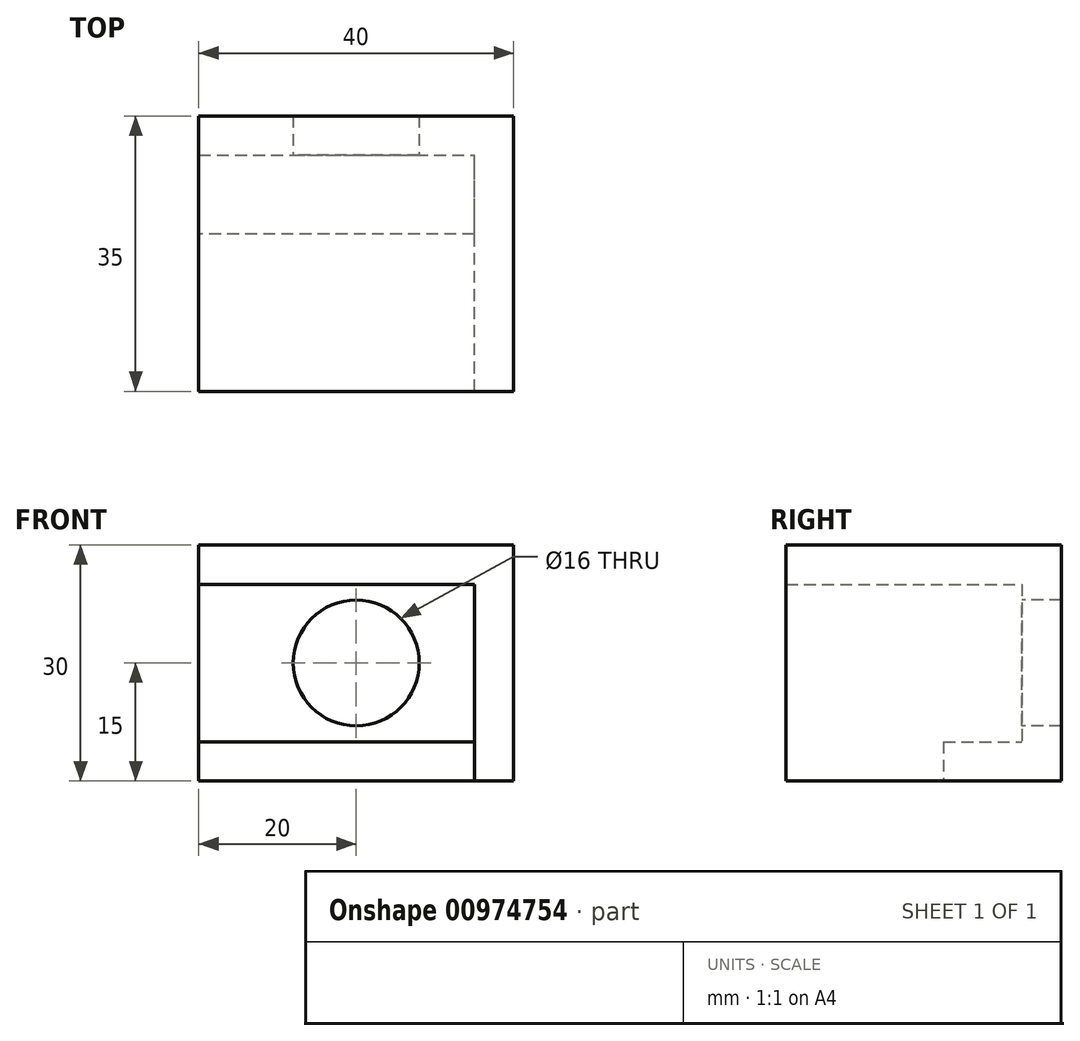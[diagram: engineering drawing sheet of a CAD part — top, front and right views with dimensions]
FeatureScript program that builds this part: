
annotation { "Feature Type Name" : "Feature", "Feature Type Description" : "" }
export const myFeature = defineFeature(function(context is Context, id is Id, definition is map)
    precondition{}
    {
        {
            var Q0;
            Q0=qCreatedBy(makeId("Front.planeOp"),FACE);
            var sketch = newSketch(context, id + "F0", { "sketchPlane" : qUnion([Q0])});
            skLineSegment(sketch, "E0.bottom", {"start": v(20, 15) * mm, "end": v(-20, 15) * mm});
            skLineSegment(sketch, "E0.top", {"start": v(20, -15) * mm, "end": v(-20, -15) * mm});
            skLineSegment(sketch, "E0.left", {"start": v(20, 15) * mm, "end": v(20, -15) * mm});
            skLineSegment(sketch, "E0.right", {"start": v(-20, 15) * mm, "end": v(-20, -15) * mm});
            skPoint(sketch, "E0.middle", {"position": v(0, 0) * mm});
            skSolve(sketch);
        }
        {
            var Q0;
            Q0 = qSketchRegion(id + "F0", true);
            extrude(context, id + "F1", {"entities" : qUnion([Q0]), "depth" : 5 * mm, "offsetDistance" : 25 * mm});
        }
        {
            var Q0;
            Q0=makeQuery(id+"F1.opExtrude","CAP_FACE",FACE,{"disambiguationData":[OSD([sQuery(id+"F0.wireOp",EDGE,"E0.bottom"),sQuery(id+"F0.wireOp",EDGE,"E0.top"),sQuery(id+"F0.wireOp",EDGE,"E0.left"),sQuery(id+"F0.wireOp",EDGE,"E0.right")])],"isStart":false});
            var sketch = newSketch(context, id + "F2", { "sketchPlane" : qUnion([Q0])});
            skCircle(sketch, "E1", {"center": v(0, 0) * mm, "radius": 8 * mm});
            skSolve(sketch);
        }
        {
            var Q0;
            Q0 = qSketchRegion(id + "F2", true);
            extrude(context, id + "F3", {"entities" : qUnion([Q0]), "operationType" : NewBodyOperationType.REMOVE, "oppositeDirection" : true, "depth" : 25 * mm, "offsetDistance" : 25 * mm});
        }
        {
            var Q0;
            Q0=makeQuery(id+"F1.opExtrude","CAP_FACE",FACE,{"disambiguationData":[OSD([sQuery(id+"F0.wireOp",EDGE,"E0.bottom"),sQuery(id+"F0.wireOp",EDGE,"E0.top"),sQuery(id+"F0.wireOp",EDGE,"E0.left"),sQuery(id+"F0.wireOp",EDGE,"E0.right")])],"isStart":false});
            var sketch = newSketch(context, id + "F4", { "sketchPlane" : qUnion([Q0])});
            skLineSegment(sketch, "E2.bottom", {"start": v(20, -15) * mm, "end": v(15, -15) * mm});
            skLineSegment(sketch, "E2.top", {"start": v(20, 15) * mm, "end": v(15, 15) * mm});
            skLineSegment(sketch, "E2.left", {"start": v(20, -15) * mm, "end": v(20, 15) * mm});
            skLineSegment(sketch, "E2.right", {"start": v(15, -15) * mm, "end": v(15, 15) * mm});
            skLineSegment(sketch, "E3.bottom", {"start": v(-20, 15) * mm, "end": v(15, 15) * mm});
            skLineSegment(sketch, "E3.top", {"start": v(-20, 10) * mm, "end": v(15, 10) * mm});
            skLineSegment(sketch, "E3.left", {"start": v(-20, 15) * mm, "end": v(-20, 10) * mm});
            skLineSegment(sketch, "E3.right", {"start": v(15, 15) * mm, "end": v(15, 10) * mm});
            skSolve(sketch);
        }
        {
            var Q0;
            Q0 = qSketchRegion(id + "F4", true);
            extrude(context, id + "F5", {"entities" : qUnion([Q0]), "operationType" : NewBodyOperationType.ADD, "depth" : 30 * mm, "offsetDistance" : 25 * mm});
        }
        {
            var Q0;
            Q0=makeQuery(id+"F1.opExtrude","CAP_FACE",FACE,{"disambiguationData":[OSD([sQuery(id+"F0.wireOp",EDGE,"E0.bottom"),sQuery(id+"F0.wireOp",EDGE,"E0.top"),sQuery(id+"F0.wireOp",EDGE,"E0.left"),sQuery(id+"F0.wireOp",EDGE,"E0.right")])],"isStart":false});
            var sketch = newSketch(context, id + "F6", { "sketchPlane" : qUnion([Q0])});
            skLineSegment(sketch, "E4.bottom", {"start": v(-20, -15) * mm, "end": v(15, -15) * mm});
            skLineSegment(sketch, "E4.top", {"start": v(-20, -10) * mm, "end": v(15, -10) * mm});
            skLineSegment(sketch, "E4.left", {"start": v(-20, -15) * mm, "end": v(-20, -10) * mm});
            skLineSegment(sketch, "E4.right", {"start": v(15, -15) * mm, "end": v(15, -10) * mm});
            skSolve(sketch);
        }
        {
            var Q0;
            Q0 = qSketchRegion(id + "F6", true);
            extrude(context, id + "F7", {"entities" : qUnion([Q0]), "operationType" : NewBodyOperationType.ADD, "depth" : 10 * mm, "offsetDistance" : 25 * mm});
        }
    });
